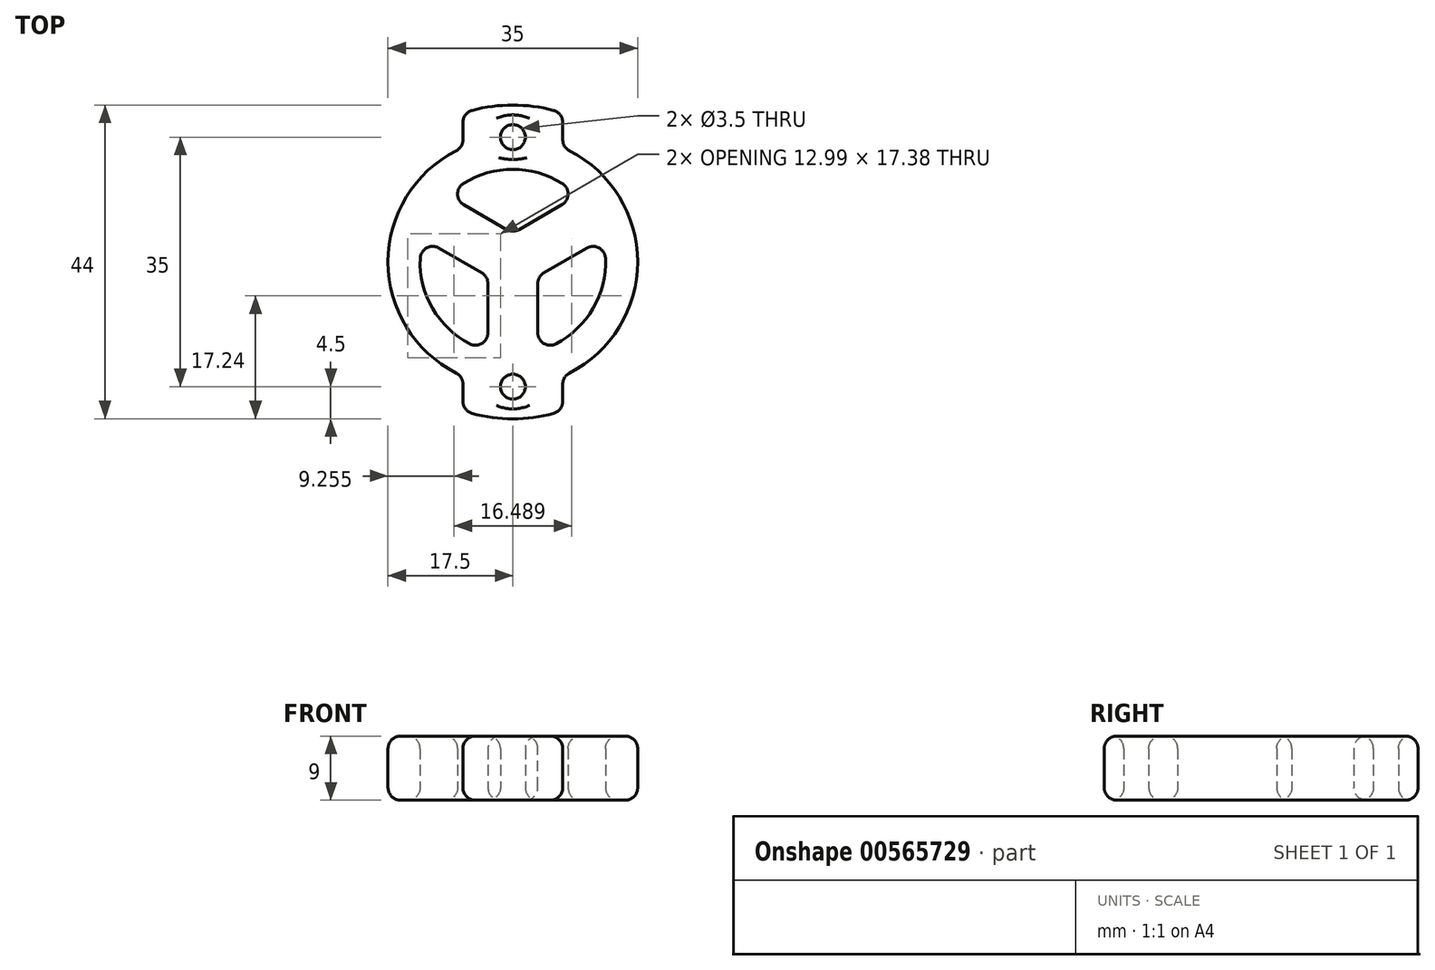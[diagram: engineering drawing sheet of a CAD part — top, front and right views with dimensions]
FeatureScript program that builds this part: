
annotation { "Feature Type Name" : "Feature", "Feature Type Description" : "" }
export const myFeature = defineFeature(function(context is Context, id is Id, definition is map)
    precondition{}
    {
        {
            var Q0;
            Q0=qCreatedBy(makeId("Top.planeOp"),FACE);
            var sketch = newSketch(context, id + "F0", { "sketchPlane" : qUnion([Q0])});
            skLineSegment(sketch, "E0", {"start": v(0, 60) * mm, "end": v(0, -60) * mm});
            skLineSegment(sketch, "E1", {"start": v(-70, 0) * mm, "end": v(70, 0) * mm});
            skArc(sketch, "E2", {"start": v(-7, 16.04) * mm, "mid": v(-17.5, 0) * mm, "end": v(-7, -16.04) * mm});
            skArc(sketch, "E3", {"start": v(-12.6, 3.23) * mm, "mid": v(-11.26, -6.5) * mm, "end": v(-3.5, -12.52) * mm});
            skLineSegment(sketch, "E4", {"start": v(0, 4.04) * mm, "end": v(-9.1, 9.3) * mm});
            skLineSegment(sketch, "E5", {"start": v(-3.5, -2.02) * mm, "end": v(-12.6, 3.23) * mm});
            skLineSegment(sketch, "E6", {"start": v(0, 4.04) * mm, "end": v(9.1, 9.3) * mm});
            skLineSegment(sketch, "E7", {"start": v(3.5, -2.02) * mm, "end": v(12.6, 3.23) * mm});
            skArc(sketch, "E8", {"start": v(3.5, -12.52) * mm, "mid": v(11.26, -6.5) * mm, "end": v(12.6, 3.23) * mm});
            skArc(sketch, "E9", {"start": v(9.1, 9.3) * mm, "mid": v(0, 13) * mm, "end": v(-9.1, 9.3) * mm});
            skArc(sketch, "E10", {"start": v(-7, -20.86) * mm, "mid": v(0, -22) * mm, "end": v(7, -20.86) * mm});
            skArc(sketch, "E11", {"start": v(7, 20.86) * mm, "mid": v(0, 22) * mm, "end": v(-7, 20.86) * mm});
            skArc(sketch, "E12", {"start": v(7, -16.04) * mm, "mid": v(17.5, 0) * mm, "end": v(7, 16.04) * mm});
            skLineSegment(sketch, "E13", {"start": v(-3.5, -2.02) * mm, "end": v(-3.5, -12.52) * mm});
            skLineSegment(sketch, "E14", {"start": v(3.5, -2.02) * mm, "end": v(3.5, -12.52) * mm});
            skCircle(sketch, "E15", {"center": v(0, 17.5) * mm, "radius": 1.75 * mm});
            skCircle(sketch, "E16", {"center": v(0, -17.5) * mm, "radius": 1.75 * mm});
            skLineSegment(sketch, "E17", {"start": v(-7, 20.86) * mm, "end": v(-7, 16.04) * mm});
            skLineSegment(sketch, "E18", {"start": v(7, 20.86) * mm, "end": v(7, 16.04) * mm});
            skLineSegment(sketch, "E19", {"start": v(-7, -16.04) * mm, "end": v(-7, -20.86) * mm});
            skLineSegment(sketch, "E20", {"start": v(7, -16.04) * mm, "end": v(7, -20.86) * mm});
            skSolve(sketch);
        }
        {
            var Q0;
            {var subQ0=sQuery(id+"F0.wireOp",EDGE,"E13");Q0=makeQuery(id+"F0.imprint","IMPRINT",FACE,{"disambiguationData":[TD([[makeQuery(id+"F0.imprint","IMPRINT",EDGE,{"derivedFrom":subQ0}),1.0]])]});}
            var Q1;
            {var subQ11=sQuery(id+"F0.wireOp",EDGE,"E14");Q1=makeQuery(id+"F0.imprint","IMPRINT",FACE,{"disambiguationData":[TD([[makeQuery(id+"F0.imprint","IMPRINT",EDGE,{"derivedFrom":subQ11}),-1.0]])]});}
            var Q2;
            {var subQ15=sQuery(id+"F0.wireOp",EDGE,"E6");Q2=makeQuery(id+"F0.imprint","IMPRINT",FACE,{"disambiguationData":[TD([[makeQuery(id+"F0.imprint","IMPRINT",EDGE,{"derivedFrom":subQ15}),-1.0]])]});}
            var Q3;
            {var subQ5=sQuery(id+"F0.wireOp",EDGE,"E4");Q3=makeQuery(id+"F0.imprint","IMPRINT",FACE,{"disambiguationData":[TD([[makeQuery(id+"F0.imprint","IMPRINT",EDGE,{"derivedFrom":subQ5}),1.0]])]});}
            extrude(context, id + "F1", {"entities" : qUnion([Q0, Q1, Q2, Q3]), "depth" : 9 * mm, "offsetDistance" : 25 * mm});
        }
        {
            var Q0;
            Q0=makeQuery(id+"F1.opExtrude","SWEPT_EDGE",EDGE,{"disambiguationData":[OSD([sQuery(id+"F0.wireOp",EDGE,"E10"),sQuery(id+"F0.wireOp",EDGE,"E20")])]});
            var Q1;
            Q1=makeQuery(id+"F1.opExtrude","SWEPT_EDGE",EDGE,{"disambiguationData":[OSD([sQuery(id+"F0.wireOp",EDGE,"E10"),sQuery(id+"F0.wireOp",EDGE,"E19")])]});
            var Q2;
            Q2=makeQuery(id+"F1.opExtrude","SWEPT_EDGE",EDGE,{"disambiguationData":[OSD([sQuery(id+"F0.wireOp",EDGE,"E12"),sQuery(id+"F0.wireOp",EDGE,"E20")])]});
            var Q3;
            Q3=makeQuery(id+"F1.opExtrude","SWEPT_EDGE",EDGE,{"disambiguationData":[OSD([sQuery(id+"F0.wireOp",EDGE,"E12"),sQuery(id+"F0.wireOp",EDGE,"E18")])]});
            var Q4;
            Q4=makeQuery(id+"F1.opExtrude","SWEPT_EDGE",EDGE,{"disambiguationData":[OSD([sQuery(id+"F0.wireOp",EDGE,"E11"),sQuery(id+"F0.wireOp",EDGE,"E18")])]});
            var Q5;
            Q5=makeQuery(id+"F1.opExtrude","SWEPT_EDGE",EDGE,{"disambiguationData":[OSD([sQuery(id+"F0.wireOp",EDGE,"E11"),sQuery(id+"F0.wireOp",EDGE,"E17")])]});
            var Q6;
            Q6=makeQuery(id+"F1.opExtrude","SWEPT_EDGE",EDGE,{"disambiguationData":[OSD([sQuery(id+"F0.wireOp",EDGE,"E2"),sQuery(id+"F0.wireOp",EDGE,"E17")])]});
            var Q7;
            Q7=makeQuery(id+"F1.opExtrude","SWEPT_EDGE",EDGE,{"disambiguationData":[OSD([sQuery(id+"F0.wireOp",EDGE,"E2"),sQuery(id+"F0.wireOp",EDGE,"E19")])]});
            var Q8;
            Q8=makeQuery(id+"F1.opExtrude","SWEPT_EDGE",EDGE,{"disambiguationData":[OSD([sQuery(id+"F0.wireOp",EDGE,"E5"),sQuery(id+"F0.wireOp",EDGE,"E13")])]});
            var Q9;
            Q9=makeQuery(id+"F1.opExtrude","SWEPT_EDGE",EDGE,{"disambiguationData":[OSD([sQuery(id+"F0.wireOp",EDGE,"E6"),sQuery(id+"F0.wireOp",EDGE,"E9")])]});
            var Q10;
            Q10=makeQuery(id+"F1.opExtrude","SWEPT_EDGE",EDGE,{"disambiguationData":[OSD([sQuery(id+"F0.wireOp",EDGE,"E7"),sQuery(id+"F0.wireOp",EDGE,"E8")])]});
            var Q11;
            Q11=makeQuery(id+"F1.opExtrude","SWEPT_EDGE",EDGE,{"disambiguationData":[OSD([sQuery(id+"F0.wireOp",EDGE,"E3"),sQuery(id+"F0.wireOp",EDGE,"E5")])]});
            var Q12;
            Q12=makeQuery(id+"F1.opExtrude","SWEPT_EDGE",EDGE,{"disambiguationData":[OSD([sQuery(id+"F0.wireOp",EDGE,"E7"),sQuery(id+"F0.wireOp",EDGE,"E14")])]});
            var Q13;
            Q13=makeQuery(id+"F1.opExtrude","SWEPT_EDGE",EDGE,{"disambiguationData":[OSD([sQuery(id+"F0.wireOp",EDGE,"E4"),sQuery(id+"F0.wireOp",EDGE,"E9")])]});
            var Q14;
            Q14=makeQuery(id+"F1.opExtrude","SWEPT_EDGE",EDGE,{"disambiguationData":[OSD([sQuery(id+"F0.wireOp",EDGE,"E8"),sQuery(id+"F0.wireOp",EDGE,"E14")])]});
            var Q15;
            Q15=makeQuery(id+"F1.opExtrude","SWEPT_EDGE",EDGE,{"disambiguationData":[OSD([sQuery(id+"F0.wireOp",EDGE,"E3"),sQuery(id+"F0.wireOp",EDGE,"E13")])]});
            var Q16;
            Q16=makeQuery(id+"F1.opExtrude","SWEPT_EDGE",EDGE,{"disambiguationData":[OSD([sQuery(id+"F0.wireOp",EDGE,"E0"),sQuery(id+"F0.wireOp",EDGE,"E4"),sQuery(id+"F0.wireOp",EDGE,"E6")])]});
            var Q17;
            Q17=makeQuery(id+"F1.opExtrude","CAP_FACE",FACE,{"disambiguationData":[OSD([sQuery(id+"F0.wireOp",EDGE,"E2"),sQuery(id+"F0.wireOp",EDGE,"E3"),sQuery(id+"F0.wireOp",EDGE,"E4"),sQuery(id+"F0.wireOp",EDGE,"E5"),sQuery(id+"F0.wireOp",EDGE,"E6"),sQuery(id+"F0.wireOp",EDGE,"E7"),sQuery(id+"F0.wireOp",EDGE,"E8"),sQuery(id+"F0.wireOp",EDGE,"E9"),sQuery(id+"F0.wireOp",EDGE,"E10"),sQuery(id+"F0.wireOp",EDGE,"E11"),sQuery(id+"F0.wireOp",EDGE,"E12"),sQuery(id+"F0.wireOp",EDGE,"E13"),sQuery(id+"F0.wireOp",EDGE,"E14"),sQuery(id+"F0.wireOp",EDGE,"E15"),sQuery(id+"F0.wireOp",EDGE,"E16"),sQuery(id+"F0.wireOp",EDGE,"E17"),sQuery(id+"F0.wireOp",EDGE,"E18"),sQuery(id+"F0.wireOp",EDGE,"E19"),sQuery(id+"F0.wireOp",EDGE,"E20")])],"isStart":false});
            var Q18;
            Q18=makeQuery(id+"F1.opExtrude","CAP_FACE",FACE,{"disambiguationData":[OSD([sQuery(id+"F0.wireOp",EDGE,"E2"),sQuery(id+"F0.wireOp",EDGE,"E3"),sQuery(id+"F0.wireOp",EDGE,"E4"),sQuery(id+"F0.wireOp",EDGE,"E5"),sQuery(id+"F0.wireOp",EDGE,"E6"),sQuery(id+"F0.wireOp",EDGE,"E7"),sQuery(id+"F0.wireOp",EDGE,"E8"),sQuery(id+"F0.wireOp",EDGE,"E9"),sQuery(id+"F0.wireOp",EDGE,"E10"),sQuery(id+"F0.wireOp",EDGE,"E11"),sQuery(id+"F0.wireOp",EDGE,"E12"),sQuery(id+"F0.wireOp",EDGE,"E13"),sQuery(id+"F0.wireOp",EDGE,"E14"),sQuery(id+"F0.wireOp",EDGE,"E15"),sQuery(id+"F0.wireOp",EDGE,"E16"),sQuery(id+"F0.wireOp",EDGE,"E17"),sQuery(id+"F0.wireOp",EDGE,"E18"),sQuery(id+"F0.wireOp",EDGE,"E19"),sQuery(id+"F0.wireOp",EDGE,"E20")])],"isStart":true});
            fillet(context, id + "F2", {"entities" : qUnion([Q0, Q1, Q2, Q3, Q4, Q5, Q6, Q7, Q8, Q9, Q10, Q11, Q12, Q13, Q14, Q15, Q16, Q17, Q18]), "radius" : (3.5 / 2) * mm, "tangentPropagation" : true, "allowEdgeOverflow" : false});
        }
    });
